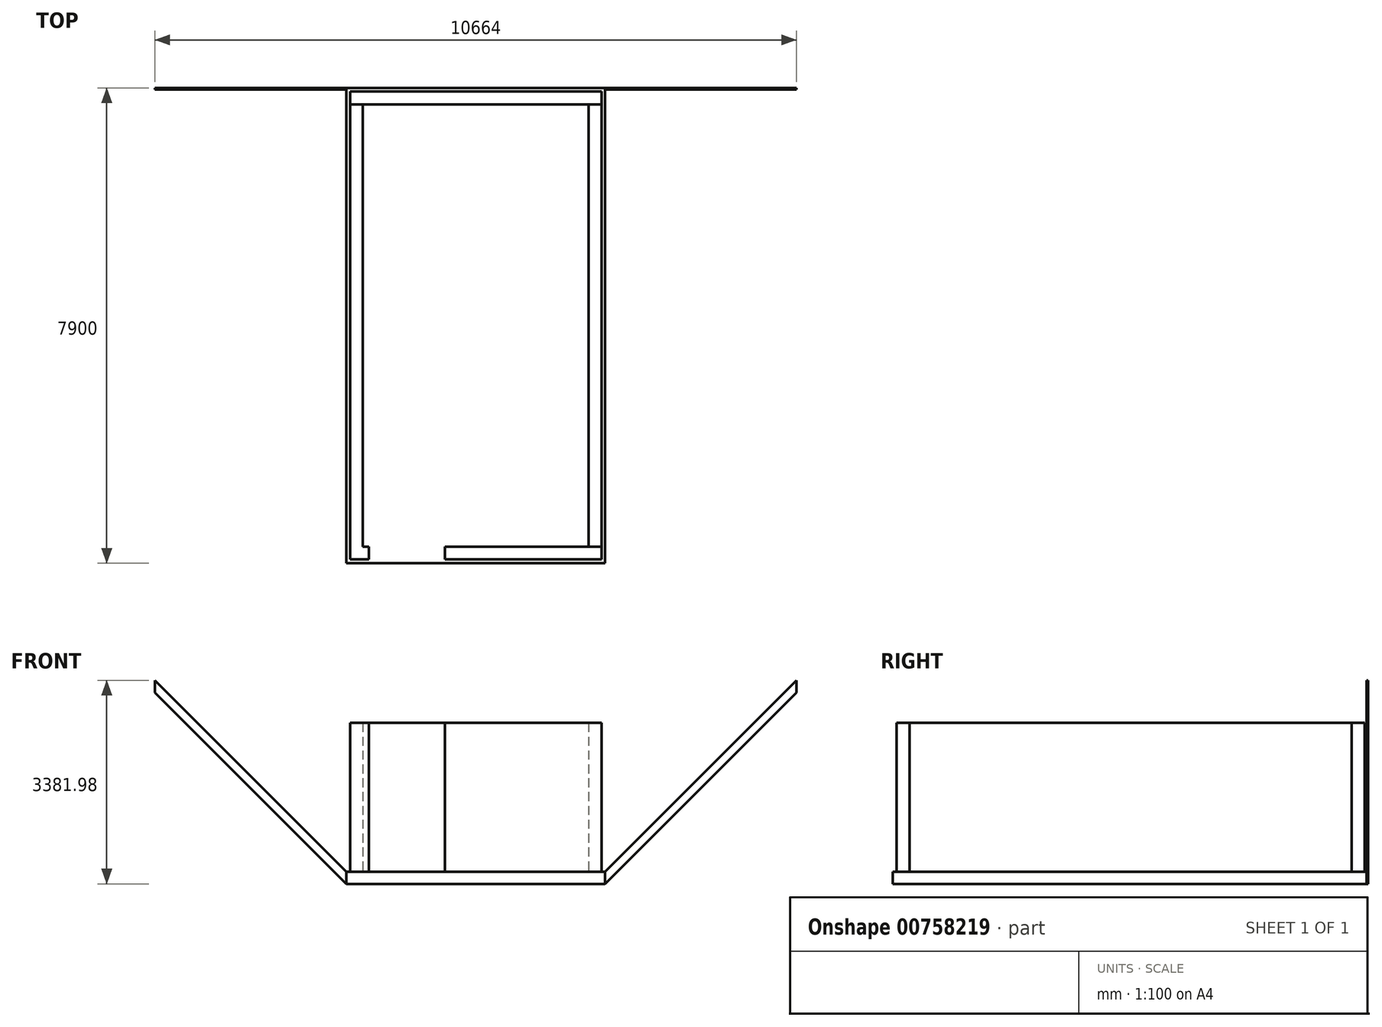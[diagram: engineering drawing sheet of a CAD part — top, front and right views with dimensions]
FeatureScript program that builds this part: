
annotation { "Feature Type Name" : "Feature", "Feature Type Description" : "" }
export const myFeature = defineFeature(function(context is Context, id is Id, definition is map)
    precondition{}
    {
        {
            var Q0;
            Q0=qCreatedBy(makeId("Top.planeOp"),FACE);
            var sketch = newSketch(context, id + "F0", { "sketchPlane" : qUnion([Q0])});
            skLineSegment(sketch, "E0.bottom", {"start": v(855.96, 1379.12) * mm, "end": v(2952.96, 1379.12) * mm});
            skLineSegment(sketch, "E0.top", {"start": v(-1347.04, 9279.12) * mm, "end": v(2952.96, 9279.12) * mm});
            skLineSegment(sketch, "E0.left", {"start": v(-1347.04, 1379.12) * mm, "end": v(-1347.04, 9279.12) * mm});
            skLineSegment(sketch, "E0.right", {"start": v(2952.96, 1379.12) * mm, "end": v(2952.96, 9279.12) * mm});
            skLineSegment(sketch, "E1", {"start": v(-1347.04, 1379.12) * mm, "end": v(855.96, 1379.12) * mm});
            skSolve(sketch);
        }
        {
            var Q0;
            Q0=makeQuery(id+"F0.imprint","IMPRINT",FACE,{"disambiguationData":[TD([[makeQuery(id+"F0.imprint","IMPRINT",EDGE,{"derivedFrom":sQuery(id+"F0.wireOp",EDGE,"E0.bottom")}),1.0]])]});
            extrude(context, id + "F1", {"entities" : qUnion([Q0]), "depth" : 200 * mm, "offsetDistance" : 25 * mm});
        }
        {
            var Q0;
            Q0=makeQuery(id+"F1.opExtrude","CAP_FACE",FACE,{"disambiguationData":[OSD([sQuery(id+"F0.wireOp",EDGE,"E0.bottom"),sQuery(id+"F0.wireOp",EDGE,"E0.top"),sQuery(id+"F0.wireOp",EDGE,"E0.left"),sQuery(id+"F0.wireOp",EDGE,"E0.right")])],"isStart":false});
            var sketch = newSketch(context, id + "F2", { "sketchPlane" : qUnion([Q0])});
            skLineSegment(sketch, "E2.bottom", {"start": v(2892.96, 1654.12) * mm, "end": v(2677.96, 1654.12) * mm});
            skLineSegment(sketch, "E2.top", {"start": v(2892.96, 9004.12) * mm, "end": v(2677.96, 9004.12) * mm});
            skLineSegment(sketch, "E2.left", {"start": v(2892.96, 1654.12) * mm, "end": v(2892.96, 9004.12) * mm});
            skLineSegment(sketch, "E2.right", {"start": v(2677.96, 1654.12) * mm, "end": v(2677.96, 9004.12) * mm});
            skSolve(sketch);
        }
        {
            var Q0;
            Q0=makeQuery(id+"F2.imprint","IMPRINT",FACE,{"disambiguationData":[TD([[makeQuery(id+"F2.imprint","IMPRINT",EDGE,{"derivedFrom":sQuery(id+"F2.wireOp",EDGE,"E2.bottom")}),-1.0]])]});
            extrude(context, id + "F3", {"entities" : qUnion([Q0]), "depth" : 2475 * mm, "offsetDistance" : 25 * mm});
        }
        {
            var Q0;
            Q0=makeQuery(id+"F1.opExtrude","CAP_FACE",FACE,{"disambiguationData":[OSD([sQuery(id+"F0.wireOp",EDGE,"E0.bottom"),sQuery(id+"F0.wireOp",EDGE,"E0.top"),sQuery(id+"F0.wireOp",EDGE,"E0.left"),sQuery(id+"F0.wireOp",EDGE,"E0.right"),sQuery(id+"F0.wireOp",EDGE,"E1")])],"isStart":false});
            var sketch = newSketch(context, id + "F4", { "sketchPlane" : qUnion([Q0])});
            skLineSegment(sketch, "E3", {"start": v(-1287.04, 9004.12) * mm, "end": v(-1287.04, 1439.12) * mm});
            skLineSegment(sketch, "E4", {"start": v(-1287.04, 1439.12) * mm, "end": v(-972.04, 1439.12) * mm});
            skLineSegment(sketch, "E5", {"start": v(-972.04, 1439.12) * mm, "end": v(-972.04, 1654.12) * mm});
            skLineSegment(sketch, "E6", {"start": v(-972.04, 1654.12) * mm, "end": v(-1072.04, 1654.12) * mm});
            skLineSegment(sketch, "E7", {"start": v(-1072.04, 1654.12) * mm, "end": v(-1072.04, 9004.12) * mm});
            skLineSegment(sketch, "E8", {"start": v(-1072.04, 9004.12) * mm, "end": v(-1287.04, 9004.12) * mm});
            skSolve(sketch);
        }
        {
            var Q0;
            Q0=makeQuery(id+"F4.imprint","IMPRINT",FACE,{"disambiguationData":[TD([[makeQuery(id+"F4.imprint","IMPRINT",EDGE,{"derivedFrom":sQuery(id+"F4.wireOp",EDGE,"E3")}),1.0]])]});
            extrude(context, id + "F5", {"entities" : qUnion([Q0]), "depth" : 2475 * mm, "offsetDistance" : 25 * mm});
        }
        {
            var Q0;
            Q0=makeQuery(id+"F1.opExtrude","CAP_FACE",FACE,{"disambiguationData":[OSD([sQuery(id+"F0.wireOp",EDGE,"E0.bottom"),sQuery(id+"F0.wireOp",EDGE,"E0.top"),sQuery(id+"F0.wireOp",EDGE,"E0.left"),sQuery(id+"F0.wireOp",EDGE,"E0.right")])],"isStart":false});
            var sketch = newSketch(context, id + "F6", { "sketchPlane" : qUnion([Q0])});
            skLineSegment(sketch, "E9.bottom", {"start": v(2892.96, 9004.12) * mm, "end": v(-1287.04, 9004.12) * mm});
            skLineSegment(sketch, "E9.top", {"start": v(2892.96, 9219.12) * mm, "end": v(-1287.04, 9219.12) * mm});
            skLineSegment(sketch, "E9.left", {"start": v(2892.96, 9004.12) * mm, "end": v(2892.96, 9219.12) * mm});
            skLineSegment(sketch, "E9.right", {"start": v(-1287.04, 9004.12) * mm, "end": v(-1287.04, 9219.12) * mm});
            skSolve(sketch);
        }
        {
            var Q0;
            Q0=makeQuery(id+"F6.imprint","IMPRINT",FACE,{"disambiguationData":[TD([[makeQuery(id+"F6.imprint","IMPRINT",EDGE,{"derivedFrom":sQuery(id+"F6.wireOp",EDGE,"E9.bottom")}),-1.0]])]});
            extrude(context, id + "F7", {"entities" : qUnion([Q0]), "depth" : 2475 * mm, "offsetDistance" : 25 * mm});
        }
        {
            var Q0;
            Q0=makeQuery(id+"F1.opExtrude","SWEPT_FACE",FACE,{"disambiguationData":[OSD([sQuery(id+"F0.wireOp",EDGE,"E0.top")])]});
            var sketch = newSketch(context, id + "F8", { "sketchPlane" : qUnion([Q0])});
            skPoint(sketch, "E10.0", {"position": v(-2952.96, 200) * mm});
            skPoint(sketch, "E11.0", {"position": v(-2952.96, 0) * mm});
            skPoint(sketch, "E12.0", {"position": v(1347.04, 200) * mm});
            skPoint(sketch, "E13.0", {"position": v(1347.04, 0) * mm});
            skLineSegment(sketch, "E14", {"start": v(-2952.96, 0) * mm, "end": v(-2952.96, 200) * mm});
            skLineSegment(sketch, "E15", {"start": v(-2952.96, 200) * mm, "end": v(-6134.94, 3381.98) * mm});
            skLineSegment(sketch, "E16", {"start": v(-2952.96, 0) * mm, "end": v(-6134.94, 3181.98) * mm});
            skLineSegment(sketch, "E17", {"start": v(-6134.94, 3181.98) * mm, "end": v(-6134.94, 3381.98) * mm});
            skLineSegment(sketch, "E18", {"start": v(1347.04, 0) * mm, "end": v(1347.04, 200) * mm});
            skLineSegment(sketch, "E19", {"start": v(1347.04, 200) * mm, "end": v(4529.02, 3381.98) * mm});
            skLineSegment(sketch, "E20", {"start": v(1347.04, 0) * mm, "end": v(4529.02, 3181.98) * mm});
            skLineSegment(sketch, "E21", {"start": v(4529.02, 3181.98) * mm, "end": v(4529.02, 3381.98) * mm});
            skSolve(sketch);
        }
        {
            var Q0;
            Q0=makeQuery(id+"F8.imprint","IMPRINT",FACE,{"disambiguationData":[TD([[makeQuery(id+"F8.imprint","IMPRINT",EDGE,{"derivedFrom":sQuery(id+"F8.wireOp",EDGE,"E14")}),-1.0]])]});
            extrude(context, id + "F9", {"entities" : qUnion([Q0]), "oppositeDirection" : true, "depth" : 25 * mm, "offsetDistance" : 25 * mm});
        }
        {
            var Q0;
            Q0=makeQuery(id+"F8.imprint","IMPRINT",FACE,{"disambiguationData":[TD([[makeQuery(id+"F8.imprint","IMPRINT",EDGE,{"derivedFrom":sQuery(id+"F8.wireOp",EDGE,"E18")}),1.0]])]});
            extrude(context, id + "F10", {"entities" : qUnion([Q0]), "oppositeDirection" : true, "depth" : 25 * mm, "offsetDistance" : 25 * mm});
        }
        {
            var Q0;
            Q0=makeQuery(id+"F1.opExtrude","CAP_FACE",FACE,{"disambiguationData":[OSD([sQuery(id+"F0.wireOp",EDGE,"E0.bottom"),sQuery(id+"F0.wireOp",EDGE,"E0.top"),sQuery(id+"F0.wireOp",EDGE,"E0.left"),sQuery(id+"F0.wireOp",EDGE,"E0.right"),sQuery(id+"F0.wireOp",EDGE,"E1")])],"isStart":false});
            var sketch = newSketch(context, id + "F11", { "sketchPlane" : qUnion([Q0])});
            skLineSegment(sketch, "E22.bottom", {"start": v(2892.96, 1654.12) * mm, "end": v(287.96, 1654.12) * mm});
            skLineSegment(sketch, "E22.top", {"start": v(2892.96, 1439.12) * mm, "end": v(287.96, 1439.12) * mm});
            skLineSegment(sketch, "E22.left", {"start": v(2892.96, 1654.12) * mm, "end": v(2892.96, 1439.12) * mm});
            skLineSegment(sketch, "E22.right", {"start": v(287.96, 1654.12) * mm, "end": v(287.96, 1439.12) * mm});
            skSolve(sketch);
        }
        {
            var Q0;
            Q0=makeQuery(id+"F11.imprint","IMPRINT",FACE,{"disambiguationData":[TD([[makeQuery(id+"F11.imprint","IMPRINT",EDGE,{"derivedFrom":sQuery(id+"F11.wireOp",EDGE,"E22.bottom")}),1.0]])]});
            extrude(context, id + "F12", {"entities" : qUnion([Q0]), "depth" : 2478 * mm, "offsetDistance" : 25 * mm});
        }
    });
